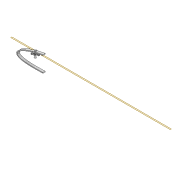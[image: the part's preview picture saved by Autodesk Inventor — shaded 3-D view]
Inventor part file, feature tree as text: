
AUTODESK INVENTOR PART (.ipt)
format: ipt  version: 2022 (Build 260153000, 153)  size: 612,864 bytes
history: native  units: mm
features: extrude x10, sketch x10, projected_geometry x7, plane x4, fillet x2, shell x1, pattern_circular x1
ambient origin geometry x8: Origin, YZ Plane, XZ Plane, XY Plane, X Axis, Y Axis, Z Axis, Center Point
bodies: Solid1 (feature_tree)
feature tree (35):
  extrude  "Extrusion1"  Depth=3.0mm
  shell  "Shell1"  Thickness=5.215mm
  plane  "Work Plane3"
  sketch  "Sketch26"  dims[d69=4.1mm d70=63.6mm]
  plane  "Work Plane4"
  extrude  "Extrusion9"  Depth=63.6mm
  plane  "Work Plane5"
  extrude  "Extrusion10"  Depth=4.2mm
  extrude  "Extrusion11"  Depth=6.0mm
  extrude  "Extrusion12"  Depth=21.0mm TaperAngle=0.0deg
  plane  "Work Plane6"
  extrude  "Extrusion13"  Depth=5.0mm
  extrude  "Extrusion15"  Depth=3.0mm TaperAngle=0.0deg
  extrude  "Extrusion16"  Depth=2.0mm
  extrude  "Extrusion17"  Depth=2.0mm
  fillet  "Fillet2"  Radius=4.0mm
  extrude  "Extrusion18"  Depth=2.0mm
  pattern_circular  "Circular Pattern1"  [2 undecoded]
  fillet  "Fillet3"  Radius=28.0mm
  sketch  "Sketch3"  dims[d0=12.0mm d1=0.0mm d2=3.0mm d68=5.215mm]
  sketch  "Sketch27"  dims[d71=12.0mm d72=4.2mm]
  projected_geometry  "Projected Loop13"
  sketch  "Sketch29"  dims[d73=63.6mm d74=6.0mm]
  sketch  "Sketch30"  dims[d75=7.0mm d76=21.0mm d77=0.0mm]
  projected_geometry  "Projected Loop14"
  sketch  "Sketch31"  dims[d78=-11.5mm d79=5.0mm]
  projected_geometry  "Projected Loop15"
  projected_geometry  "Projected Loop16"
  projected_geometry  "Projected Loop17"
  sketch  "Sketch33"  dims[d80=10.0mm d83=3.0mm d84=0.0mm]
  sketch  "Sketch34"  dims[d86=0.65mm d87=2.0mm]
  projected_geometry  "Projected Loop18"
  sketch  "Sketch35"  dims[d88=2.0mm d89=4.0mm d90=4.0mm]
  projected_geometry  "Projected Loop19"
  sketch  "Sketch36"  dims[d91=3.0mm d92=0.0mm d93=12.0mm d94=7.0mm d95=0.0mm d96=28.0mm d98=9.0mm d99=0.0mm d103=200.0mm d104=100.0mm d105=0.0mm d106=7.0mm d107=4.1mm d108=7.0mm d109=2.0mm d110=0.0mm d111=2.0mm d112=0.0mm d113=2.0mm d114=95.0mm d115=10.0mm d116=0.0mm d117=20.0mm d118=180.0deg d120=2.0mm]
note: 2 required parameter values undecoded (feature->parameter linkage not recoverable at this tier; creation-order binding heuristic only, values carry confidence <= 0.55)
